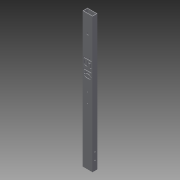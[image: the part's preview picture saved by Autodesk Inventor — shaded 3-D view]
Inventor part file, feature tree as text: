
AUTODESK INVENTOR PART (.ipt)
format: ipt  version: 2013 (Build 170138000, 138)  size: 237,056 bytes
history: native  units: in
note: dims shown in document units (in); Inventor stores cm internally (conversion verified against a paired STEP export)
features: sketch x7, extrude x6, hole x1
ambient origin geometry x8: Origin, YZ Plane, XZ Plane, XY Plane, X Axis, Y Axis, Z Axis, Center Point
bodies: Solid1 (feature_tree)
feature tree (14):
  extrude  "Extrusion1"  Depth=1.0in
  extrude  "Extrusion2"  Depth=0.75in
  extrude  "Extrusion4"  Depth=1.0in
  extrude  "Extrusion6"  Depth=0.5in
  extrude  "Extrusion9"  Depth=0.5in TaperAngle=0.0deg
  hole  "Hole1"  [1 undecoded]
  extrude  "Extrusion10"  Depth=2.0in
  sketch  "Sketch1"  dims[d0=2.0in d1=1.0in]
  sketch  "Sketch2"  dims[d2=1.75in d3=0.75in]
  sketch  "Sketch4"  dims[d4=24.0in d5=0.0in d6=1.0in]
  sketch  "Sketch6"  dims[d7=1.0in d8=0.5in]
  sketch  "Sketch8"  dims[d9=24.0in d10=0.0in d25=0.5in d26=0.0in]
  sketch  "Sketch9"  dims[d35=2.5in d36=0.0in d49=13.543in]
  sketch  "Sketch10"  dims[d50=90.0deg d51=2.0in d52=180.0deg d53=0.25in d54=0.25in d55=2.0in d56=0.0in d57=3.313in d58=1.5in d59=90.0deg d60=0.25in d61=0.75in d62=0.375in d63=0.25in d64=0.5635in d65=1.0in d66=0.8108in d67=0.5in d68=90.0deg d69=3.75in d75=0.25in d76=150.0deg d77=0.25in d78=0.25in d79=1.0in d80=0.875in d81=0.25in d82=0.625in d83=0.25in d87=45.0deg d88=0.442in d89=135.0deg d90=0.442in d95=1.5in d96=0.25in d97=0.5in d98=150.0deg d103=135.0deg d105=135.0deg d107=45.0deg d109=45.0deg d114=0.5in d115=0.5in d118=0.0625in d119=0.25in d120=0.25in d121=0.25in d122=0.25in d123=0.5in d124=0.5in d125=0.5in d126=0.5in d127=0.5in d128=0.25in d129=1.0in d130=0.25in d131=0.0in]
note: 1 required parameter value undecoded (feature->parameter linkage not recoverable at this tier; creation-order binding heuristic only, values carry confidence <= 0.55)
